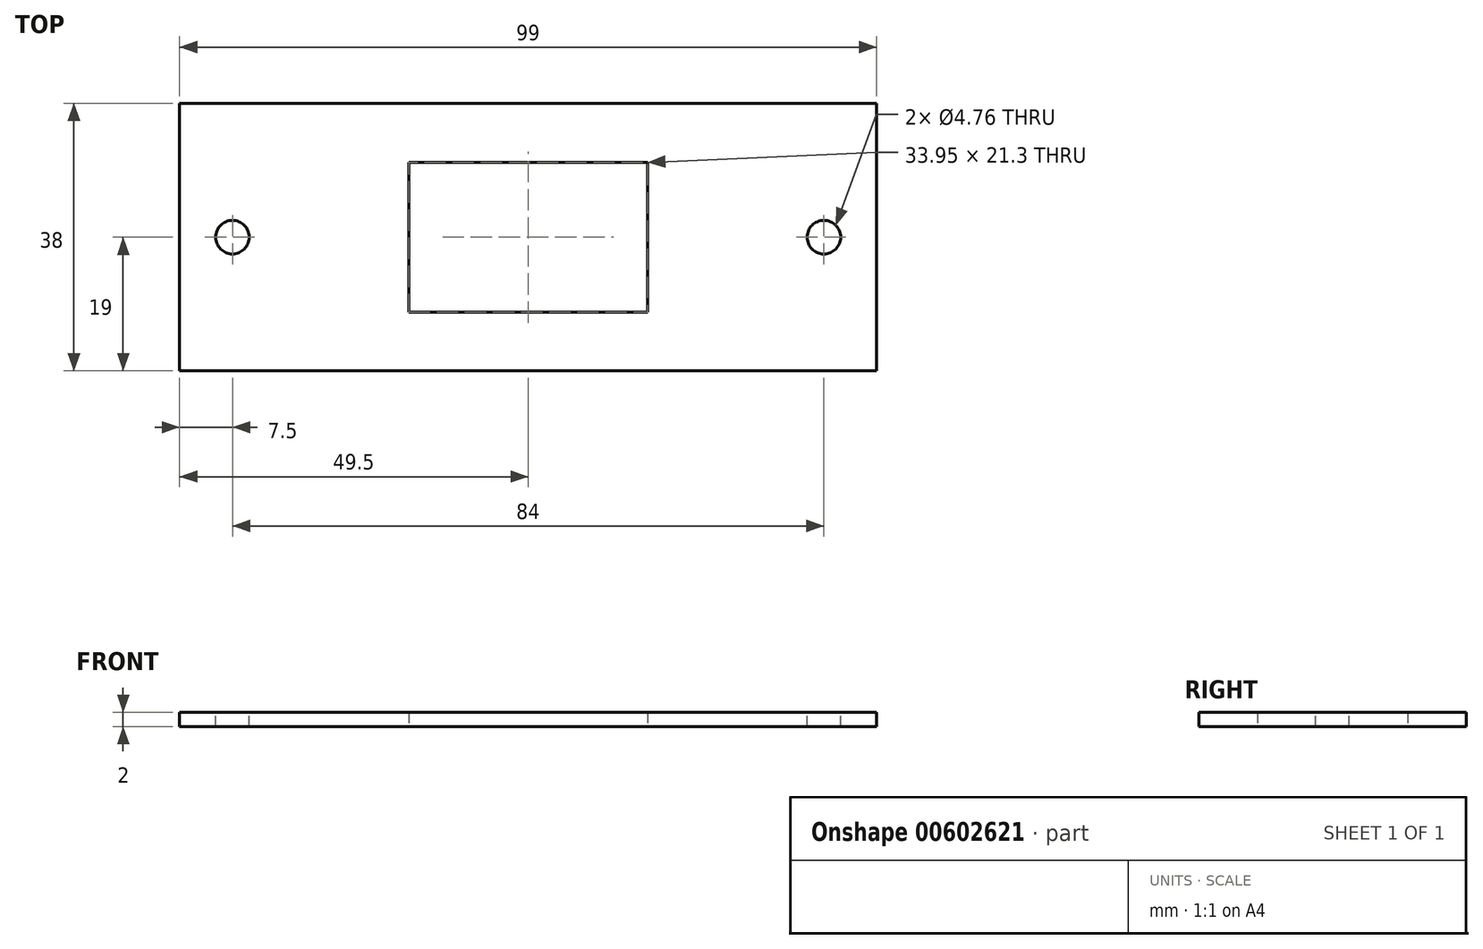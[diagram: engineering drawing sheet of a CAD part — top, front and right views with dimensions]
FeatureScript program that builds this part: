
annotation { "Feature Type Name" : "Feature", "Feature Type Description" : "" }
export const myFeature = defineFeature(function(context is Context, id is Id, definition is map)
    precondition{}
    {
        {
            var Q0;
            Q0=qCreatedBy(makeId("Top.planeOp"),FACE);
            var sketch = newSketch(context, id + "F0", { "sketchPlane" : qUnion([Q0])});
            skLineSegment(sketch, "E0.0", {"start": v(99, 0) * mm, "end": v(99, 38) * mm});
            skLineSegment(sketch, "E0.2", {"start": v(0, 0) * mm, "end": v(0, 38) * mm});
            skLineSegment(sketch, "E0.3", {"start": v(0, 38) * mm, "end": v(99, 38) * mm});
            skLineSegment(sketch, "E1", {"start": v(0, 0) * mm, "end": v(99, 0) * mm});
            skLineSegment(sketch, "E2.bottom", {"start": v(32.52, 8.35) * mm, "end": v(66.48, 8.35) * mm});
            skLineSegment(sketch, "E2.top", {"start": v(32.52, 29.65) * mm, "end": v(66.48, 29.65) * mm});
            skLineSegment(sketch, "E2.left", {"start": v(32.52, 8.35) * mm, "end": v(32.52, 29.65) * mm});
            skLineSegment(sketch, "E2.right", {"start": v(66.47, 8.35) * mm, "end": v(66.47, 29.65) * mm});
            skLineSegment(sketch, "E3", {"start": v(49.5, 8.35) * mm, "end": v(49.5, 0) * mm, "construction": true});
            skPoint(sketch, "E3.endSnap0", {"position": v(49.5, 8.35) * mm});
            skLineSegment(sketch, "E4", {"start": v(0, 19) * mm, "end": v(32.52, 19) * mm, "construction": true});
            skLineSegment(sketch, "E5", {"start": v(49.5, 29.65) * mm, "end": v(49.5, 38) * mm, "construction": true});
            skLineSegment(sketch, "E6", {"start": v(99, 19) * mm, "end": v(66.48, 19) * mm, "construction": true});
            skSolve(sketch);
        }
        {
            var Q0;
            Q0 = qSketchRegion(id + "F0", true);
            extrude(context, id + "F1", {"entities" : qUnion([Q0]), "depth" : 2 * mm, "offsetDistance" : 25 * mm});
        }
        {
            var Q0;
            Q0=makeQuery(id+"F1.opExtrude","CAP_FACE",FACE,{"disambiguationData":[OSD([sQuery(id+"F0.wireOp",EDGE,"AiZ4gYoa-msa6-boio-fEdS-XP4aReER9jLD.bottom"),sQuery(id+"F0.wireOp",EDGE,"AiZ4gYoa-msa6-boio-fEdS-XP4aReER9jLD.top"),sQuery(id+"F0.wireOp",EDGE,"AiZ4gYoa-msa6-boio-fEdS-XP4aReER9jLD.left"),sQuery(id+"F0.wireOp",EDGE,"AiZ4gYoa-msa6-boio-fEdS-XP4aReER9jLD.right"),sQuery(id+"F0.wireOp",EDGE,"E0.0"),sQuery(id+"F0.wireOp",EDGE,"E0.1"),sQuery(id+"F0.wireOp",EDGE,"E0.2"),sQuery(id+"F0.wireOp",EDGE,"E0.3")])],"isStart":false});
            var sketch = newSketch(context, id + "F2", { "sketchPlane" : qUnion([Q0])});
            skPoint(sketch, "E7.0", {"position": v(15, 19) * mm});
            skPoint(sketch, "E8.0", {"position": v(84, 19) * mm});
            skPoint(sketch, "E9.0", {"position": v(0, 19) * mm});
            skPoint(sketch, "E10.0", {"position": v(99, 19) * mm});
            skLineSegment(sketch, "E11", {"start": v(0, 19) * mm, "end": v(15, 19) * mm, "construction": true});
            skLineSegment(sketch, "E12", {"start": v(84, 19) * mm, "end": v(99, 19) * mm, "construction": true});
            skCircle(sketch, "E13", {"center": v(7.5, 19) * mm, "radius": 2.38 * mm});
            skCircle(sketch, "E14", {"center": v(91.5, 19) * mm, "radius": 2.38 * mm});
            skSolve(sketch);
        }
        {
            var Q0;
            Q0 = qSketchRegion(id + "F2", true);
            extrude(context, id + "F3", {"entities" : qUnion([Q0]), "operationType" : NewBodyOperationType.REMOVE, "endBound" : BoundingType.THROUGH_ALL, "oppositeDirection" : true, "depth" : 25 * mm, "offsetDistance" : 25 * mm});
        }
    });
